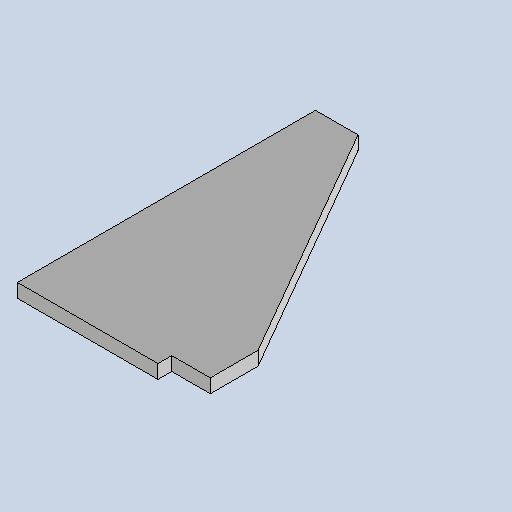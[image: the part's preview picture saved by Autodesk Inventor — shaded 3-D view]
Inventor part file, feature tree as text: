
AUTODESK INVENTOR PART (.ipt)
format: ipt  version: 2025 (Build 290162010, 162A)  size: 176,128 bytes
history: native  units: mm
features: other x2, sheet_metal_op x1, sketch x1
ambient origin geometry x8: Origin, YZ Plane, XZ Plane, XY Plane, X Axis, Y Axis, Z Axis, Center Point
bodies: Body1 (feature_tree)
feature tree (4):
  sheet_metal_op  "Face2"
  sketch  "Sketch3"  dims[d18=10.0mm d19=150.0mm d29=10.0mm d31=60.0deg d32=20.0mm d34=48.0mm]
  other  "Plate3"
  other  "Definition1"
